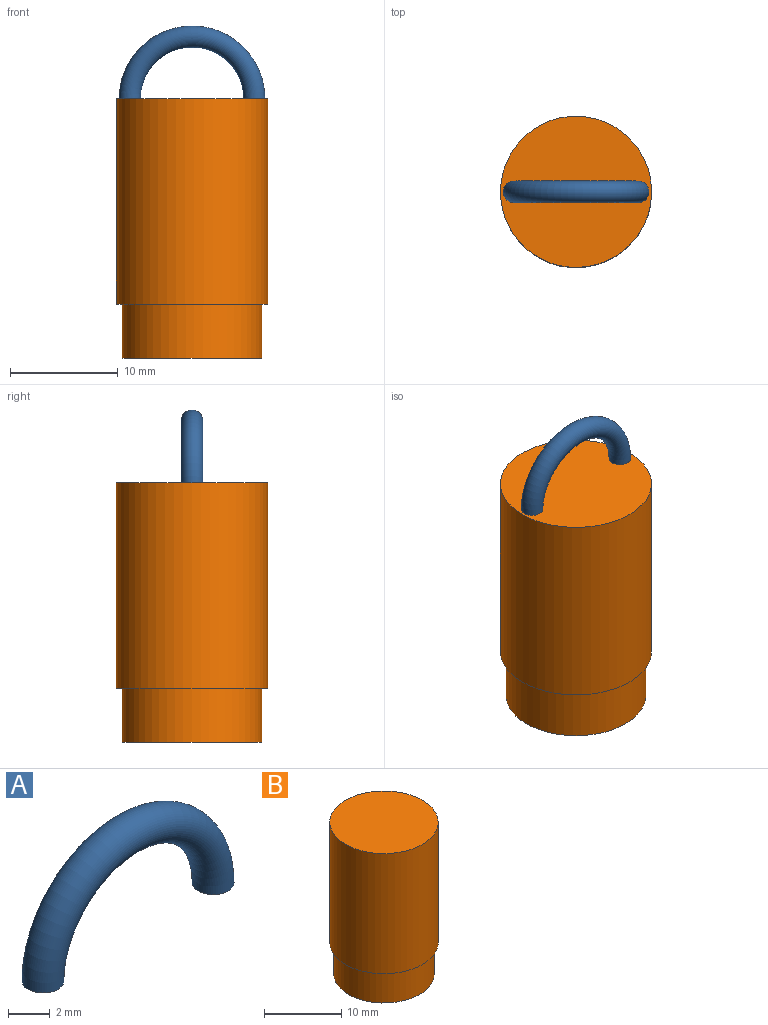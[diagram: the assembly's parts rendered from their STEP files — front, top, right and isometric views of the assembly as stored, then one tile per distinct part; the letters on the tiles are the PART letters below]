
ASSEMBLY  parts=2 mates=1
PART A: 3 faces, bbox 14.6x2x7.3 mm
  f0: plane 2x2mm, normal (0,0,-1), area 3.1mm2, adj f2
  f1: plane 2x2mm, normal (0,0,-1), area 3.1mm2, adj f2
  f2: torus R=5.75mm, axis (0,-1,0), area 113.5mm2, adj f0,f1
PART B: 7 faces, bbox 14x14x24 mm
  f0: plane 12.94x12.94mm, normal (0,0,-1), area 18.5mm2, adj f2,f3
  f1: plane 12x12mm, normal (0,0,-1), area 113.1mm2, adj f2
  f2: cylinder r=6mm len=23mm, axis (0,0,-1), area 867.1mm2, adj f0,f1
  f3: cylinder r=6.47mm len=12.94mm, axis (0,0,-1), area 203.3mm2, adj f0,f4
  f4: plane 14x14mm, normal (0,0,-1), area 22.4mm2, adj f3,f6
  f5: plane 14x14mm, normal (0,0,1), area 153.9mm2, adj f6
  f6: cylinder r=7mm len=19mm, axis (0,0,-1), area 835.7mm2, adj f4,f5
PLACE A t=(-12.14,-9.73,0.95)mm
PLACE B t=(-6.39,-9.73,0.95)mm
MATE fastened A.f0 <-> B.f5  axis (0,0,-1) through (-0.64,-9.73,0.95)mm
